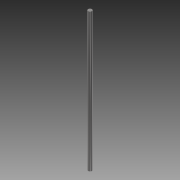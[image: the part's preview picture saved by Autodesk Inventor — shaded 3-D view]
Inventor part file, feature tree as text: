
AUTODESK INVENTOR PART (.ipt)
format: ipt  version: 2013 (Build 170138000, 138)  size: 78,848 bytes
history: native  units: mm
features: extrude x1, sketch x1
ambient origin geometry x8: Origin, YZ Plane, XZ Plane, XY Plane, X Axis, Y Axis, Z Axis, Center Point
bodies: Solid1 (feature_tree)
feature tree (2):
  extrude  "Extrusion1"  Depth=301.0mm TaperAngle=0.0deg
  sketch  "Sketch1"  dims[d0=8.0mm d2=301.0mm d3=0.0mm]
